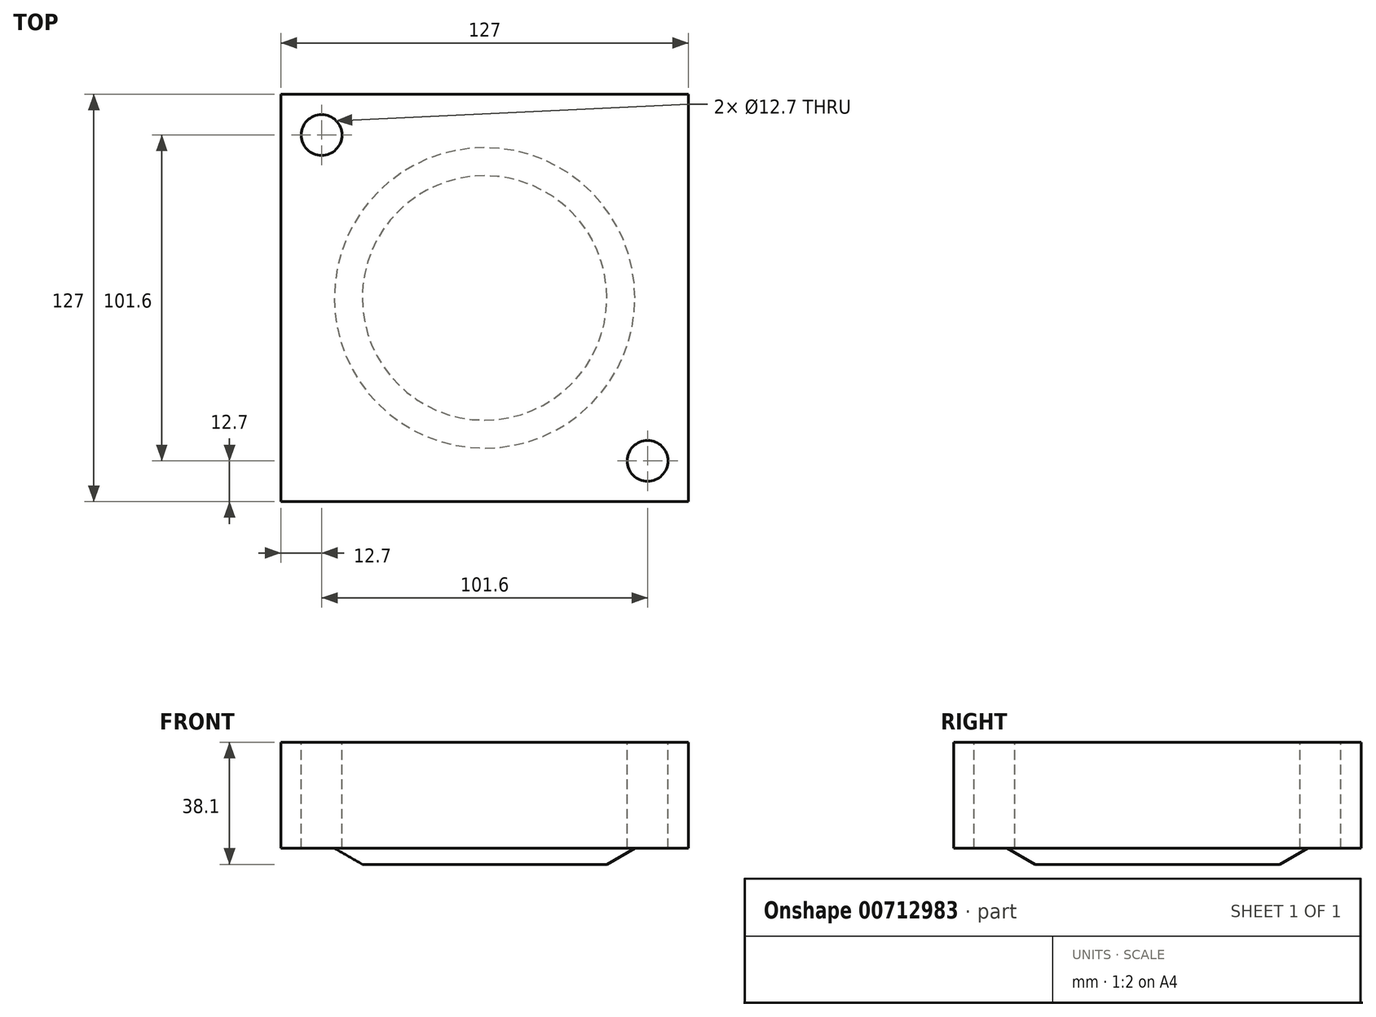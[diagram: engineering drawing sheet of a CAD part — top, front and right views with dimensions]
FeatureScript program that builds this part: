
annotation { "Feature Type Name" : "Feature", "Feature Type Description" : "" }
export const myFeature = defineFeature(function(context is Context, id is Id, definition is map)
    precondition{}
    {
        {
            var Q0;
            Q0=qCreatedBy(makeId("Front.planeOp"),FACE);
            var sketch = newSketch(context, id + "F0", { "sketchPlane" : qUnion([Q0])});
            skLineSegment(sketch, "E0", {"start": v(0, 0) * mm, "end": v(38.1, 0) * mm});
            skLineSegment(sketch, "E1", {"start": v(0, 2.29) * mm, "end": v(38.1, 2.29) * mm});
            skLineSegment(sketch, "E2", {"start": v(38.1, 2.29) * mm, "end": v(46.84, 7.33) * mm});
            skLineSegment(sketch, "E3", {"start": v(46.84, 7.33) * mm, "end": v(50.8, 7.33) * mm});
            skLineSegment(sketch, "E4", {"start": v(50.8, 7.33) * mm, "end": v(91.42, 7.33) * mm});
            skLineSegment(sketch, "E5", {"start": v(91.42, 7.33) * mm, "end": v(91.42, 0) * mm});
            skLineSegment(sketch, "E6", {"start": v(91.42, 0) * mm, "end": v(38.1, 0) * mm});
            skLineSegment(sketch, "E7", {"start": v(0, 2.29) * mm, "end": v(0, 0) * mm});
            skLineSegment(sketch, "E8", {"start": v(0, 3.57) * mm, "end": v(0, -1.1) * mm, "construction": true});
            skSolve(sketch);
        }
        {
            var Q0;
            Q0=qCreatedBy(makeId("Front.planeOp"),FACE);
            var sketch = newSketch(context, id + "F1", { "sketchPlane" : qUnion([Q0])});
            skLineSegment(sketch, "E9.bottom", {"start": v(-63.5, 0) * mm, "end": v(63.5, 0) * mm});
            skLineSegment(sketch, "E9.left", {"start": v(-63.5, 0) * mm, "end": v(-63.5, 40.39) * mm});
            skLineSegment(sketch, "E9.right", {"start": v(63.5, 0) * mm, "end": v(63.5, 40.39) * mm});
            skLineSegment(sketch, "E10", {"start": v(-63.5, 40.39) * mm, "end": v(0, 40.39) * mm});
            skLineSegment(sketch, "E11", {"start": v(0, 40.39) * mm, "end": v(63.5, 40.39) * mm});
            skSolve(sketch);
        }
        {
            var Q0;
            Q0 = qSketchRegion(id + "F1", true);
            extrude(context, id + "F2", {"entities" : qUnion([Q0]), "endBound" : BoundingType.SYMMETRIC, "depth" : 127 * mm, "offsetDistance" : 25.4 * mm});
        }
        {
            var Q0;
            Q0 = qSketchRegion(id + "F0", true);
            var Q1;
            Q1=sQuery(id+"F0.wireOp",EDGE,"E7");
            revolve(context, id + "F3", {"operationType" : NewBodyOperationType.REMOVE, "surfaceOperationType" : NewSurfaceOperationType.NEW, "entities" : qUnion([Q0]), "axis" : qUnion([Q1]), "revolveType" : RevolveType.FULL, "oppositeDirection" : true});
        }
        {
            var Q0;
            Q0=qCreatedBy(makeId("Top.planeOp"),FACE);
            var sketch = newSketch(context, id + "F4", { "sketchPlane" : qUnion([Q0])});
            skCircle(sketch, "E12", {"center": v(-50.8, 50.8) * mm, "radius": 6.35 * mm});
            skCircle(sketch, "E13", {"center": v(50.8, -50.8) * mm, "radius": 6.35 * mm});
            skSolve(sketch);
        }
        {
            var Q0;
            Q0 = qSketchRegion(id + "F4", true);
            extrude(context, id + "F5", {"entities" : qUnion([Q0]), "operationType" : NewBodyOperationType.REMOVE, "endBound" : BoundingType.SYMMETRIC, "oppositeDirection" : true, "depth" : 101.6 * mm, "offsetDistance" : 25.4 * mm});
        }
    });
